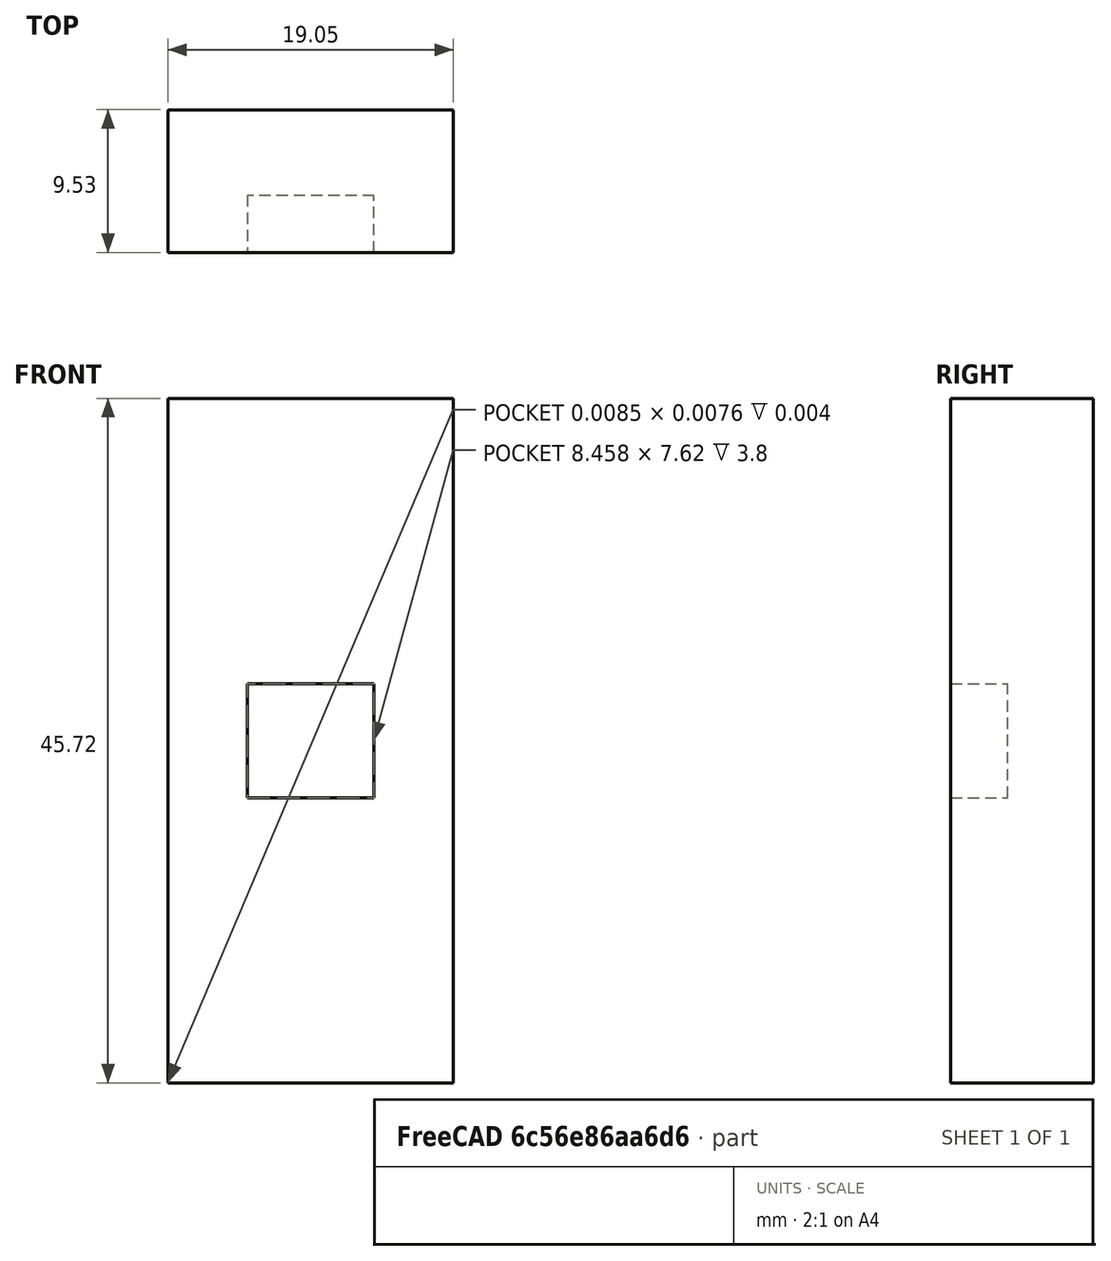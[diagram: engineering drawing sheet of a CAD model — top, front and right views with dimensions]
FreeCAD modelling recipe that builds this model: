
FCSTD DOCUMENT  (FreeCAD 0.21R33694 (Git))
Label: dielectric-loading
License: All rights reserved
LicenseURL: http://en.wikipedia.org/wiki/All_rights_reserved
objects: Part::Part2DObjectPython×6, App::FeaturePython×4, Part::FeaturePython×3, Part::Extrusion×2
note: 11 computed .brp shape members not serialized (recipe doc carries the construction recipe); baked Part::Feature solids carry a one-line shape summary decoded from their .brp

FEATURE [Part::Part2DObjectPython] Rectangle  # Draft 2D object (typed FeaturePython)
  Area = 181.451
  ChamferSize = 0
  Columns = 1
  FilletRadius = 0
  Height = 9.525
  Length = 19.05
  MakeFace = true
  Rows = 1
FEATURE [Part::Part2DObjectPython] Rectangle001  # Draft 2D object (typed FeaturePython)
  Area = 32.1404
  ChamferSize = 0
  Columns = 1
  FilletRadius = 0
  Height = 3.8
  Length = 8.458
  MakeFace = true
  Placement = pos=(5.296,0,0) rot=(0,0,1;0rad)
  Rows = 1
FEATURE [Part::Extrusion] Extrude
  Base = -> Rectangle001
  Dir = (0,0,1)
  DirMode = 2
  FaceMakerClass = Part::FaceMakerBullseye
  LengthFwd = 7.62
  LengthRev = 0
  Placement = pos=(0,0,19.05) rot=(0,0,1;0rad)
  Solid = false
  Symmetric = false
FEATURE [Part::Extrusion] Extrude001
  Base = -> Rectangle
  Dir = (0,0,1)
  DirMode = 2
  FaceMakerClass = Part::FaceMakerBullseye
  LengthFwd = 45.72
  LengthRev = 0
  Solid = false
  Symmetric = false
FEATURE [Part::FeaturePython] BooleanFragments  # WARN: FeaturePython — macro-defined, semantics opaque (R4)
  Mode = 0
  Objects = -> [Extrude,Extrude001]
  Tolerance = 0
FEATURE [Part::FeaturePython] BooleanFragments001  # WARN: FeaturePython — macro-defined, semantics opaque (R4)
  Mode = 0
  Objects = -> [BooleanFragments]
  Tolerance = 0
FEATURE [Part::FeaturePython] Clone  label="scaled"  # Draft clone (typed FeaturePython)
  AttacherType = Attacher::AttachEngine3D
  Fuse = false
  Objects = -> [BooleanFragments]
  Scale = (0.001,0.001,0.001)
FEATURE [Part::Part2DObjectPython] Rectangle002  label="_P1"  # Draft 2D object (typed FeaturePython)
  Area = 0.000181451
  ChamferSize = 0
  Columns = 1
  FilletRadius = 0
  Height = 0.009525
  Length = 0.01905
  MakeFace = true
  Rows = 1
FEATURE [Part::Part2DObjectPython] Rectangle003  label="_P2"  # Draft 2D object (typed FeaturePython)
  Area = 0.000181451
  ChamferSize = 0
  Columns = 1
  FilletRadius = 0
  Height = 0.009525
  Length = 0.01905
  MakeFace = true
  Placement = pos=(0,0,0.04572) rot=(0,0,1;0rad)
  Rows = 1
FEATURE [Part::Part2DObjectPython] Line  label="_PV1"  # Draft 2D object (typed FeaturePython)
  Area = 0
  ChamferSize = 0
  Closed = false
  End = (0.009525,0.009525,0)
  FilletRadius = 0
  Length = 0.009525
  MakeFace = true
  Placement = pos=(0.009525,0,0) rot=(0,0,1;0rad)
  Points = (2) [(0,0,0),(0,0.009525,0)]
  Start = (0.009525,0,0)
  Subdivisions = 0
FEATURE [Part::Part2DObjectPython] Line001  label="_PV2"  # Draft 2D object (typed FeaturePython)
  Area = 0
  ChamferSize = 0
  Closed = false
  End = (0.009525,0.009525,0.04572)
  FilletRadius = 0
  Length = 0.009525
  MakeFace = true
  Placement = pos=(0.009525,0,0.04572) rot=(0,0,1;0rad)
  Points = (2) [(0,0,0),(0,0.009525,0)]
  Start = (0.009525,0,0.04572)
  Subdivisions = 0
FEATURE [App::FeaturePython] Text  label="_S1(PV){1}"  # WARN: FeaturePython — macro-defined, semantics opaque (R4)
  Placement = pos=(0.0284767,0.000942234,0) rot=(0,0,1;0rad)
  Text = .
FEATURE [App::FeaturePython] Text001  label="_S2(PV){2}"  # WARN: FeaturePython — macro-defined, semantics opaque (R4)
  Placement = pos=(0.0284767,0.000942234,0) rot=(0,0,1;0rad)
  Text = .
FEATURE [App::FeaturePython] Text002  label="_M1(1,voltage){V1}"  # WARN: FeaturePython — macro-defined, semantics opaque (R4)
  Placement = pos=(0.0284767,0.000942234,0) rot=(0,0,1;0rad)
  Text = .
FEATURE [App::FeaturePython] Text003  label="_M2(2,voltage){V2}"  # WARN: FeaturePython — macro-defined, semantics opaque (R4)
  Placement = pos=(0.0284767,0.000942234,0) rot=(0,0,1;0rad)
  Text = .
